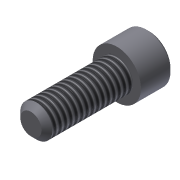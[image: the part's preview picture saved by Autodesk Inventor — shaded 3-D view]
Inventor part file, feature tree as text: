
AUTODESK INVENTOR PART (.ipt)
format: ipt  version: 2013 (Build 170138000, 138)  size: 109,568 bytes
history: native  units: in
note: dims shown in document units (in); Inventor stores cm internally (conversion verified against a paired STEP export)
features: extrude x3, sketch x3, chamfer x2, thread x1
ambient origin geometry x8: Origin, YZ Plane, XZ Plane, XY Plane, X Axis, Y Axis, Z Axis, Center Point
bodies: Solid1 (feature_tree)
feature tree (9):
  extrude  "Extrusion1"  Depth=0.315in TaperAngle=0.0deg
  extrude  "Extrusion2"  Depth=0.1181in TaperAngle=0.0deg
  extrude  "Extrusion3"  Depth=0.0591in TaperAngle=0.0deg
  thread  "Thread1"  [1 undecoded]
  chamfer  "Chamfer1"  [1 undecoded]
  chamfer  "Chamfer2"  [1 undecoded]
  sketch  "Sketch1"  dims[d0=0.1181in d1=0.315in d2=0.0in]
  sketch  "Sketch2"  dims[d3=0.1772in d4=0.1181in d5=0.0in]
  sketch  "Sketch3"  dims[d6=0.0984in d7=0.0591in d8=0.0in d9=0.8661in d10=0.0in d11=0.02in d12=0.125in d13=45.0deg d15=0.0098in d16=0.0787in d17=45.0deg]
note: 3 required parameter values undecoded (feature->parameter linkage not recoverable at this tier; creation-order binding heuristic only, values carry confidence <= 0.55)
